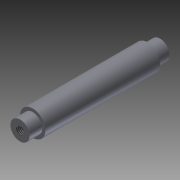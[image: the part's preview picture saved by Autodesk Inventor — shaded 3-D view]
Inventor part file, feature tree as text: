
AUTODESK INVENTOR PART (.ipt)
format: ipt  version: 2012 (Build 160160000, 160)  size: 96,768 bytes
history: native  units: in
note: dims shown in document units (in); Inventor stores cm internally (conversion verified against a paired STEP export)
features: extrude x6, sketch x3, plane x2, thread x1
ambient origin geometry x8: Origin, YZ Plane, XZ Plane, XY Plane, X Axis, Y Axis, Z Axis, Center Point
bodies: Solid1 (feature_tree)
feature tree (12):
  extrude  "Extrusion1"  Depth=3.25in TaperAngle=0.0deg
  plane  "Work Plane4"
  sketch  "Sketch4"  dims[d14=-0.5in d17=-0.5in]
  plane  "Work Plane5"
  sketch  "Sketch5"  dims[d24=0.375in d25=1.0in d26=0.0in d27=0.375in d28=1.0in d29=0.0in d30=0.25in d31=0.0in d32=0.25in d33=0.0in d35=0.164in d36=0.136in d37=0.25in d38=0.0in d41=1.0in d42=0.0in]
  extrude  "Extrusion6"  [1 undecoded]
  extrude  "Extrusion7"  Depth=1.0in TaperAngle=0.0deg
  extrude  "Extrusion8"  Depth=0.375in
  extrude  "Extrusion9"  Depth=1.0in TaperAngle=0.0deg
  extrude  "Extrusion10"  Depth=0.25in TaperAngle=0.0deg
  thread  "Thread6"  [1 undecoded]
  sketch  "Sketch1"  dims[d0=0.5in d1=3.25in d2=0.0in]
note: 2 required parameter values undecoded (feature->parameter linkage not recoverable at this tier; creation-order binding heuristic only, values carry confidence <= 0.55)
